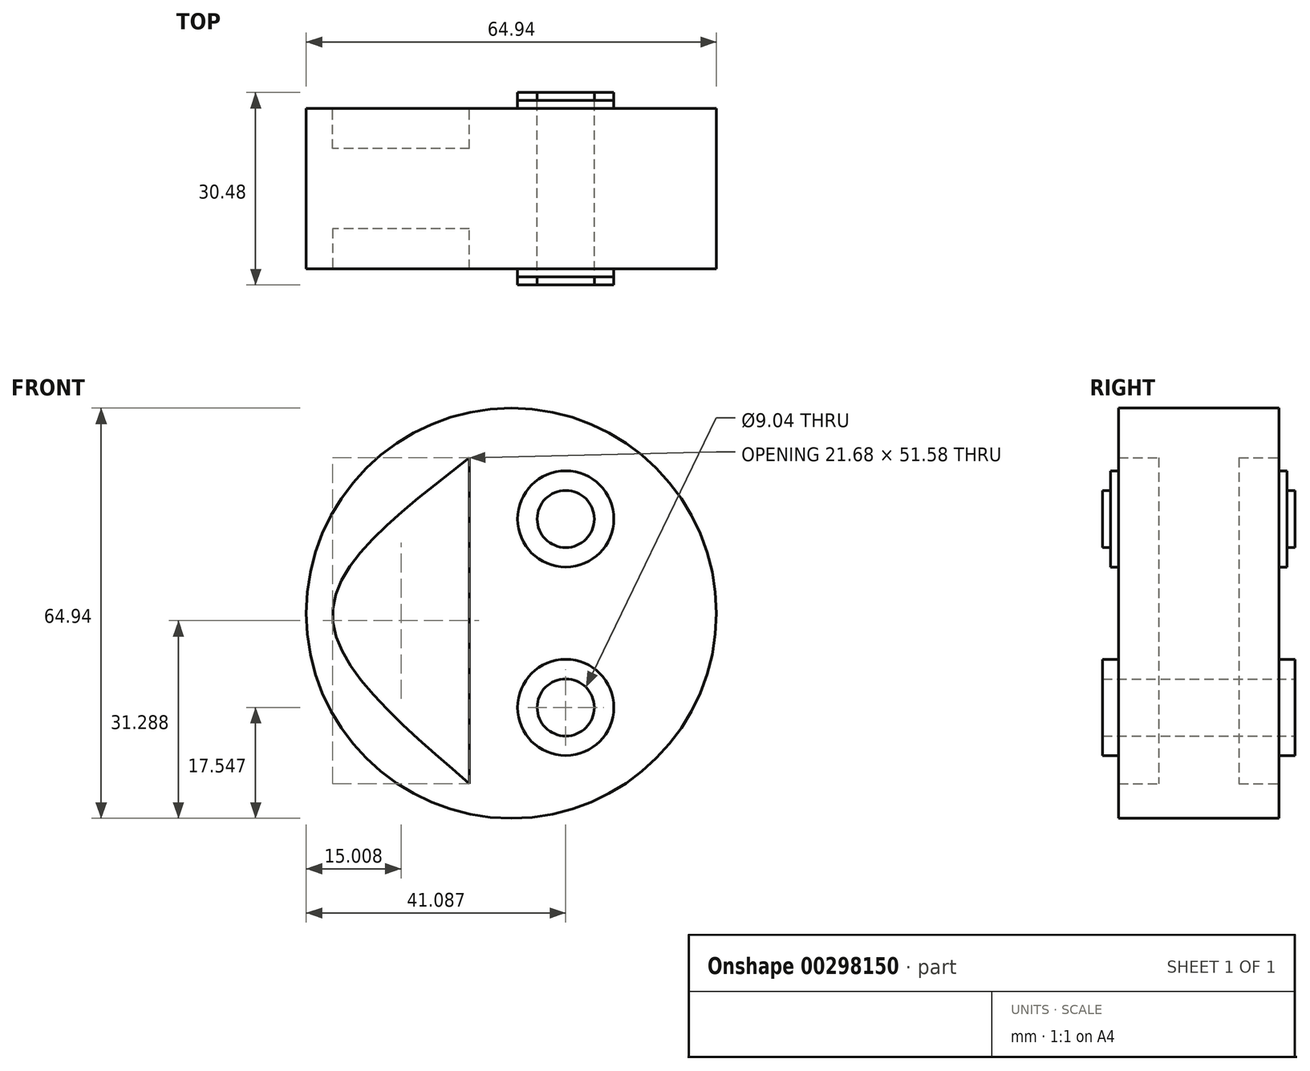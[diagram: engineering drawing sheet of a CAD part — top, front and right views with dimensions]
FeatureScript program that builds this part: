
annotation { "Feature Type Name" : "Feature", "Feature Type Description" : "" }
export const myFeature = defineFeature(function(context is Context, id is Id, definition is map)
    precondition{}
    {
        {
            var Q0;
            Q0=qCreatedBy(makeId("Front.planeOp"),FACE);
            var sketch = newSketch(context, id + "F0", { "sketchPlane" : qUnion([Q0])});
            skCircle(sketch, "E0", {"center": v(0, 0) * mm, "radius": 32.47 * mm});
            skLineSegment(sketch, "E1", {"start": v(-6.62, 24.6) * mm, "end": v(-6.62, -26.97) * mm});
            skFitSpline(sketch, "E2", {"points": [v(-6.62, 24.6) * mm, v(-28.3, 0) * mm, v(-6.62, -26.97) * mm], "startDerivative": vector(-62.55, -49.1) * mm, "endDerivative": vector(61.97, -54.04) * mm});
            skCircle(sketch, "E3", {"center": v(8.62, 14.92) * mm, "radius": 7.62 * mm});
            skCircle(sketch, "E4", {"center": v(8.62, -14.92) * mm, "radius": 7.62 * mm});
            skCircle(sketch, "E5", {"center": v(8.62, 14.92) * mm, "radius": 4.52 * mm});
            skCircle(sketch, "E6", {"center": v(8.62, -14.92) * mm, "radius": 4.52 * mm});
            skSolve(sketch);
        }
        {
            var Q0;
            Q0=makeQuery(id+"F0.imprint","IMPRINT",FACE,{"disambiguationData":[TD([[makeQuery(id+"F0.imprint","IMPRINT",EDGE,{"derivedFrom":sQuery(id+"F0.wireOp",EDGE,"E1")}),-1.0]])]});
            extrude(context, id + "F1", {"entities" : qUnion([Q0]), "endBound" : BoundingType.SYMMETRIC, "depth" : 12.7 * mm});
        }
        {
            var Q0;
            Q0=makeQuery(id+"F0.imprint","IMPRINT",FACE,{"disambiguationData":[TD([[makeQuery(id+"F0.imprint","IMPRINT",EDGE,{"derivedFrom":sQuery(id+"F0.wireOp",EDGE,"E0")}),1.0]])]});
            extrude(context, id + "F2", {"entities" : qUnion([Q0]), "operationType" : NewBodyOperationType.ADD, "endBound" : BoundingType.SYMMETRIC, "depth" : 25.4 * mm});
        }
        {
            var Q0;
            Q0=makeQuery(id+"F0.imprint","IMPRINT",FACE,{"disambiguationData":[TD([[makeQuery(id+"F0.imprint","IMPRINT",EDGE,{"derivedFrom":sQuery(id+"F0.wireOp",EDGE,"E4")}),1.0]])]});
            var Q1;
            Q1=makeQuery(id+"F0.imprint","IMPRINT",FACE,{"disambiguationData":[TD([[makeQuery(id+"F0.imprint","IMPRINT",EDGE,{"derivedFrom":sQuery(id+"F0.wireOp",EDGE,"E3")}),1.0]])]});
            extrude(context, id + "F3", {"entities" : qUnion([Q0, Q1]), "operationType" : NewBodyOperationType.ADD, "endBound" : BoundingType.SYMMETRIC, "depth" : 27.94 * mm});
        }
        {
            var Q0;
            Q0=makeQuery(id+"F0.imprint","IMPRINT",FACE,{"disambiguationData":[TD([[makeQuery(id+"F0.imprint","IMPRINT",EDGE,{"derivedFrom":sQuery(id+"F0.wireOp",EDGE,"E6")}),-1.0]])]});
            var Q1;
            Q1=makeQuery(id+"F0.imprint","IMPRINT",FACE,{"disambiguationData":[TD([[makeQuery(id+"F0.imprint","IMPRINT",EDGE,{"derivedFrom":sQuery(id+"F0.wireOp",EDGE,"E5")}),1.0]])]});
            extrude(context, id + "F4", {"entities" : qUnion([Q0, Q1]), "operationType" : NewBodyOperationType.ADD, "endBound" : BoundingType.SYMMETRIC, "depth" : 30.48 * mm});
        }
    });
